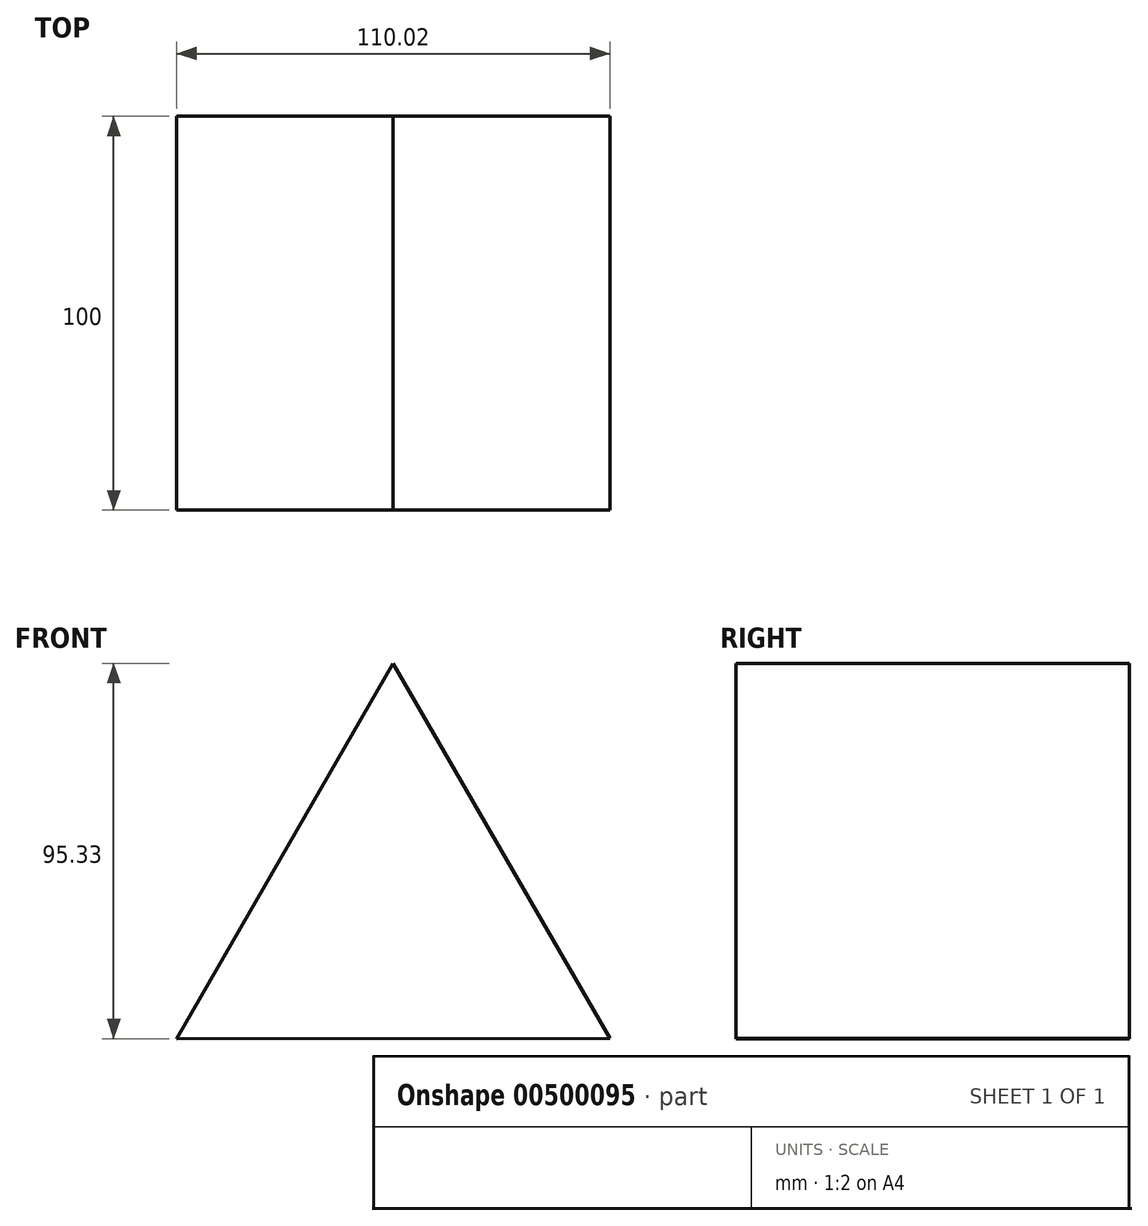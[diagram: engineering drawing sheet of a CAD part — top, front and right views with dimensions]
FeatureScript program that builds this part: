
annotation { "Feature Type Name" : "Feature", "Feature Type Description" : "" }
export const myFeature = defineFeature(function(context is Context, id is Id, definition is map)
    precondition{}
    {
        {
            var Q0;
            Q0=qCreatedBy(makeId("Front.planeOp"),FACE);
            var sketch = newSketch(context, id + "F0", { "sketchPlane" : qUnion([Q0])});
            skCircle(sketch, "E0.cCircle", {"center": v(0, 0) * mm, "radius": 63.52 * mm, "construction": true});
            skLineSegment(sketch, "E0.0", {"start": v(-0.06, 63.52) * mm, "end": v(55.04, -31.7) * mm});
            skLineSegment(sketch, "E0.1", {"start": v(55.04, -31.7) * mm, "end": v(-54.98, -31.81) * mm});
            skLineSegment(sketch, "E0.2", {"start": v(-54.98, -31.81) * mm, "end": v(-0.06, 63.52) * mm});
            skSolve(sketch);
        }
        {
            var Q0;
            Q0=makeQuery(id+"F0.imprint","IMPRINT",FACE,{"disambiguationData":[TD([[makeQuery(id+"F0.imprint","IMPRINT",EDGE,{"derivedFrom":sQuery(id+"F0.wireOp",EDGE,"E0.0")}),-1.0]])]});
            extrude(context, id + "F1", {"entities" : qUnion([Q0]), "endBound" : BoundingType.SYMMETRIC, "depth" : 100 * mm});
        }
    });
